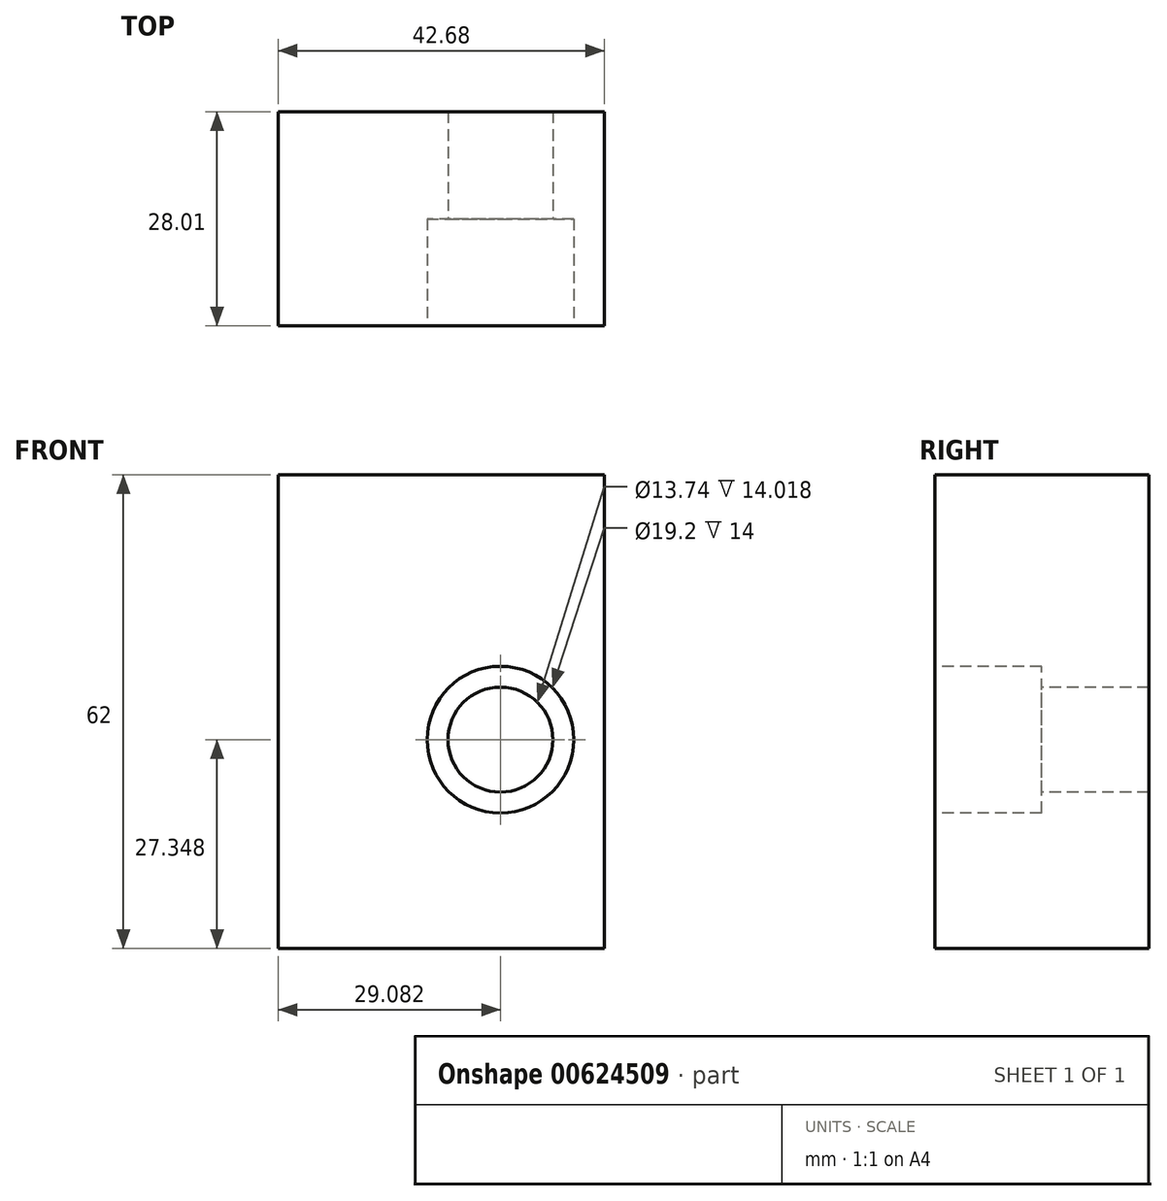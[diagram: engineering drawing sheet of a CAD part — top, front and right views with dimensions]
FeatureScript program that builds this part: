
annotation { "Feature Type Name" : "Feature", "Feature Type Description" : "" }
export const myFeature = defineFeature(function(context is Context, id is Id, definition is map)
    precondition{}
    {
        {
            var Q0;
            Q0=qCreatedBy(makeId("Top.planeOp"),FACE);
            var sketch = newSketch(context, id + "F0", { "sketchPlane" : qUnion([Q0])});
            skLineSegment(sketch, "E0.bottom", {"start": v(-42.68, 32.13) * mm, "end": v(0, 32.13) * mm});
            skLineSegment(sketch, "E0.top", {"start": v(-42.68, 4.12) * mm, "end": v(0, 4.12) * mm});
            skLineSegment(sketch, "E0.left", {"start": v(-42.68, 32.13) * mm, "end": v(-42.68, 4.12) * mm});
            skLineSegment(sketch, "E0.right", {"start": v(0, 32.13) * mm, "end": v(0, 4.12) * mm});
            skSolve(sketch);
        }
        {
            var Q0;
            Q0=makeQuery(id+"F0.imprint","IMPRINT",FACE,{"disambiguationData":[TD([[makeQuery(id+"F0.imprint","IMPRINT",EDGE,{"derivedFrom":sQuery(id+"F0.wireOp",EDGE,"E0.bottom")}),-1.0]])]});
            extrude(context, id + "F1", {"entities" : qUnion([Q0]), "depth" : 62 * mm, "offsetDistance" : 25 * mm});
        }
        {
            var Q0;
            Q0=makeQuery(id+"F1.opExtrude","SWEPT_FACE",FACE,{"disambiguationData":[OSD([sQuery(id+"F0.wireOp",EDGE,"E0.top")])]});
            var sketch = newSketch(context, id + "F2", { "sketchPlane" : qUnion([Q0])});
            skPoint(sketch, "E1", {"position": v(-13.6, 27.35) * mm});
            skSolve(sketch);
        }
        {
            var Q0;
            Q0=sQuery(id+"F2.wireOp",VERTEX,"E1");
            var Q1;
            Q1=makeQuery(id+"F1.opExtrude","SWEPT_BODY",BODY,{"disambiguationData":[OSD([sQuery(id+"F0.wireOp",EDGE,"E0.bottom"),sQuery(id+"F0.wireOp",EDGE,"E0.top"),sQuery(id+"F0.wireOp",EDGE,"E0.left"),sQuery(id+"F0.wireOp",EDGE,"E0.right")])]});
            hole(context, id + "F3", {"style" : HoleStyle.C_BORE, "endStyle" : HoleEndStyle.THROUGH, "holeDiameter" : 13.74 * mm, "cBoreDiameter" : 19.2 * mm, "cBoreDepth" : 14 * mm, "majorDiameter" : 5 * mm, "isTappedThrough" : true, "tappedDepth" : 12 * mm, "tapClearance" : 3, "startFromSketch" : true, "locations" : qUnion([Q0]), "scope" : qUnion([Q1])});
        }
    });
